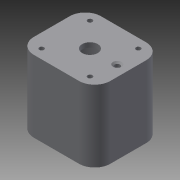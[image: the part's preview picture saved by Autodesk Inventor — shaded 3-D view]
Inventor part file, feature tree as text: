
AUTODESK INVENTOR PART (.ipt)
format: ipt  version: 2015 (Build 190159000, 159)  size: 146,944 bytes
history: native  units: mm
features: extrude x3, sketch x3, fillet x1, chamfer x1
ambient origin geometry x8: Origin, YZ Plane, XZ Plane, XY Plane, X Axis, Y Axis, Z Axis, Center Point
bodies: Solid1 (feature_tree)
feature tree (8):
  extrude  "Extrusion1"  Depth=45.0mm
  extrude  "Extrusion3"  Depth=2.0mm
  fillet  "Fillet1"  Radius=49.0mm
  chamfer  "Chamfer1"  Distance=49.0mm
  extrude  "Extrusion4"  Depth=43.0mm TaperAngle=0.0deg
  sketch  "Sketch1"  dims[d0=39.0mm d1=45.0mm]
  sketch  "Sketch2"  dims[d2=2.0mm d3=2.0mm d4=49.0mm]
  sketch  "Sketch3"  dims[d5=43.0mm d6=49.0mm d7=43.0mm d8=0.0mm d9=10.0mm d12=12.5mm d13=3.5mm d14=21.5mm d15=3.0mm d16=0.0mm d17=10.0mm d19=1.0mm d20=2.0mm d21=45.0deg d22=31.0mm d23=31.0mm d24=3.0mm d25=3.0mm d26=3.0mm d27=3.0mm d28=57.5mm d29=0.0mm]
